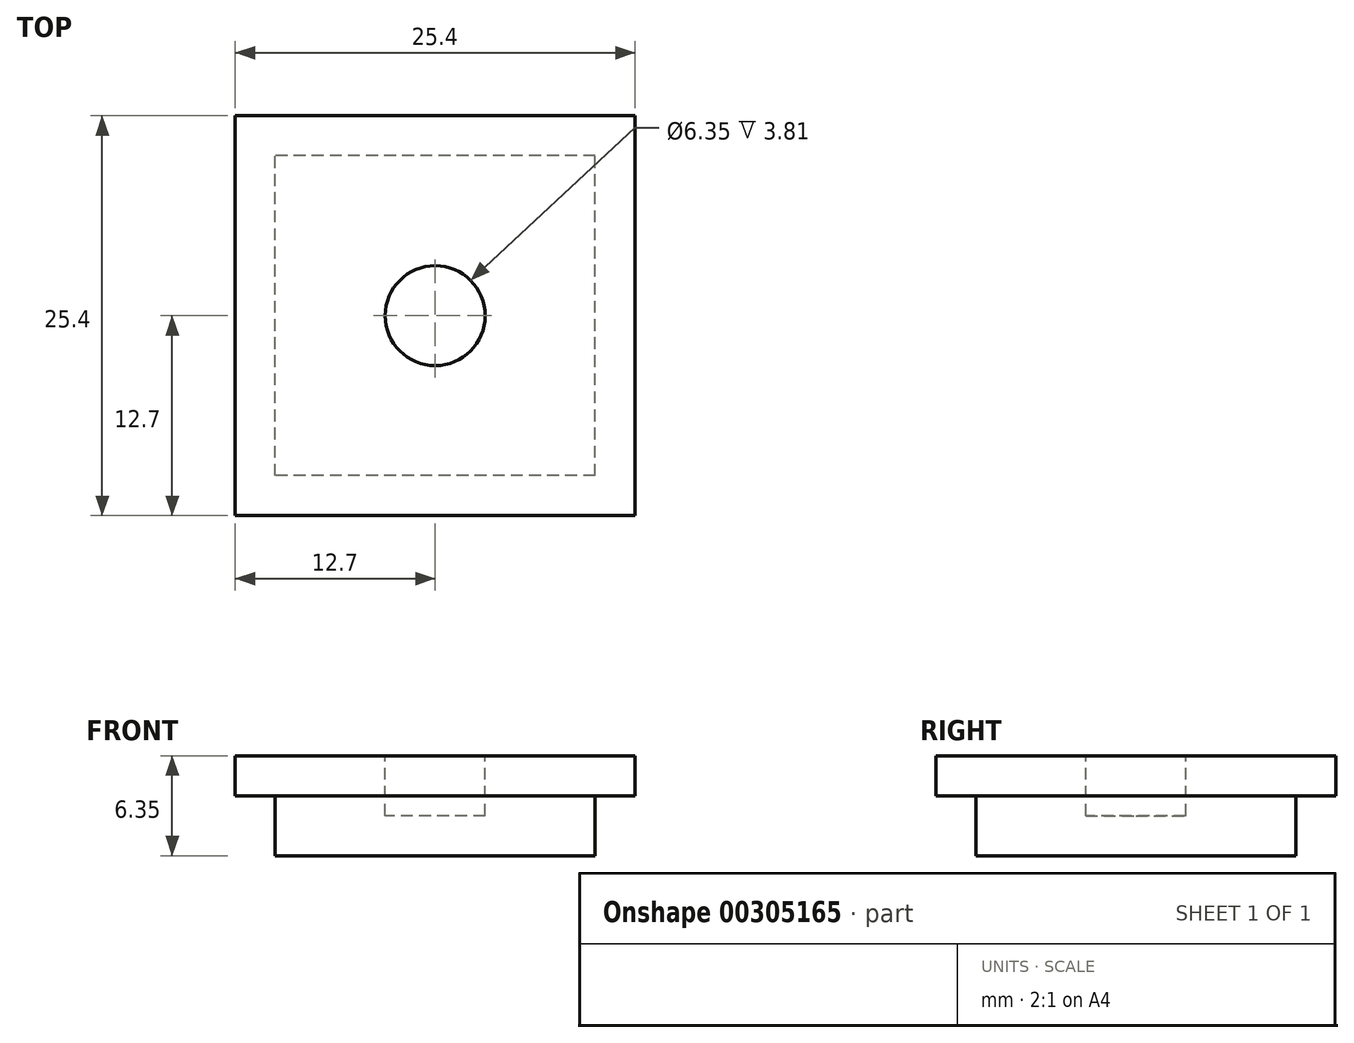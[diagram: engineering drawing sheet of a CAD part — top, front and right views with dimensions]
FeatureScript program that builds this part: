
annotation { "Feature Type Name" : "Feature", "Feature Type Description" : "" }
export const myFeature = defineFeature(function(context is Context, id is Id, definition is map)
    precondition{}
    {
        {
            var Q0;
            Q0=qCreatedBy(makeId("Top.planeOp"),FACE);
            var sketch = newSketch(context, id + "F0", { "sketchPlane" : qUnion([Q0])});
            skLineSegment(sketch, "E0.bottom", {"start": v(12.7, 12.7) * mm, "end": v(-12.7, 12.7) * mm});
            skLineSegment(sketch, "E0.top", {"start": v(12.7, -12.7) * mm, "end": v(-12.7, -12.7) * mm});
            skLineSegment(sketch, "E0.left", {"start": v(12.7, 12.7) * mm, "end": v(12.7, -12.7) * mm});
            skLineSegment(sketch, "E0.right", {"start": v(-12.7, 12.7) * mm, "end": v(-12.7, -12.7) * mm});
            skPoint(sketch, "E0.middle", {"position": v(0, 0) * mm});
            skSolve(sketch);
        }
        {
            var Q0;
            Q0=makeQuery(id+"F0.imprint","IMPRINT",FACE,{"disambiguationData":[TD([[makeQuery(id+"F0.imprint","IMPRINT",EDGE,{"derivedFrom":sQuery(id+"F0.wireOp",EDGE,"E0.bottom")}),1.0]])]});
            extrude(context, id + "F1", {"entities" : qUnion([Q0]), "depth" : 2.54 * mm});
        }
        {
            var Q0;
            Q0=makeQuery(id+"F1.opExtrude","CAP_FACE",FACE,{"disambiguationData":[OSD([sQuery(id+"F0.wireOp",EDGE,"E0.bottom"),sQuery(id+"F0.wireOp",EDGE,"E0.top"),sQuery(id+"F0.wireOp",EDGE,"E0.left"),sQuery(id+"F0.wireOp",EDGE,"E0.right")])],"isStart":true});
            var sketch = newSketch(context, id + "F2", { "sketchPlane" : qUnion([Q0])});
            skLineSegment(sketch, "E1.bottom", {"start": v(10.16, 10.16) * mm, "end": v(-10.16, 10.16) * mm});
            skLineSegment(sketch, "E1.top", {"start": v(10.16, -10.16) * mm, "end": v(-10.16, -10.16) * mm});
            skLineSegment(sketch, "E1.left", {"start": v(10.16, 10.16) * mm, "end": v(10.16, -10.16) * mm});
            skLineSegment(sketch, "E1.right", {"start": v(-10.16, 10.16) * mm, "end": v(-10.16, -10.16) * mm});
            skPoint(sketch, "E1.middle", {"position": v(0, 0) * mm});
            skSolve(sketch);
        }
        {
            var Q0;
            Q0=makeQuery(id+"F2.imprint","IMPRINT",FACE,{"disambiguationData":[TD([[makeQuery(id+"F2.imprint","IMPRINT",EDGE,{"derivedFrom":sQuery(id+"F2.wireOp",EDGE,"E1.bottom")}),1.0]])]});
            extrude(context, id + "F3", {"entities" : qUnion([Q0]), "operationType" : NewBodyOperationType.ADD, "depth" : 3.8 * mm});
        }
        {
            var Q0;
            Q0=makeQuery(id+"F1.opExtrude","CAP_FACE",FACE,{"disambiguationData":[OSD([sQuery(id+"F0.wireOp",EDGE,"E0.bottom"),sQuery(id+"F0.wireOp",EDGE,"E0.top"),sQuery(id+"F0.wireOp",EDGE,"E0.left"),sQuery(id+"F0.wireOp",EDGE,"E0.right")])],"isStart":false});
            var sketch = newSketch(context, id + "F4", { "sketchPlane" : qUnion([Q0])});
            skCircle(sketch, "E2", {"center": v(0, 0) * mm, "radius": 3.18 * mm});
            skSolve(sketch);
        }
        {
            var Q0;
            Q0=makeQuery(id+"F4.imprint","IMPRINT",FACE,{"disambiguationData":[TD([[makeQuery(id+"F4.imprint","IMPRINT",EDGE,{"derivedFrom":sQuery(id+"F4.wireOp",EDGE,"E2")}),1.0]])]});
            extrude(context, id + "F5", {"entities" : qUnion([Q0]), "operationType" : NewBodyOperationType.REMOVE, "oppositeDirection" : true, "depth" : 3.8 * mm});
        }
    });
